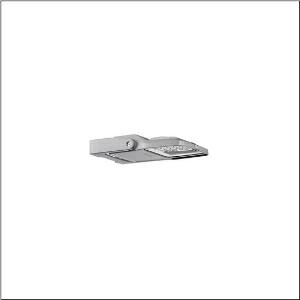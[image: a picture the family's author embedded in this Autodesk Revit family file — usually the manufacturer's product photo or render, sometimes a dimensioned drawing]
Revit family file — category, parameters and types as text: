
# Revit family: floodlight_fl_21_iq_micro___pl64_5xa7761a4e2a_05f9
name_source: partatom
category: Lighting Fixtures
units: mm (PartAtom-declared; Revit-internal decimal feet)

## family parameters
Cut with Voids When Loaded = No
Host = Face
Light Source = No
Part Type = Normal
Room Calculation Point = No
Round Connector Dimension = Use Diameter
Shared = No

## types (1)
- --- (1 x LED, 2980 lm, 23.1 W, 4000K)
    Apparent Load = 23 VA
    CIE Flux Codes = 28 80 98 100 100
    Color Rendering = 70
    Color Temperature = 4000K
    Default Elevation = 1800 mm
    Description = Floodlight FL 21 iQ micro, floodlight, primary light control with lens, of PMMA, primary optical cover: protective disc, of toughened safety glass, transparent, light distribution: PL64, light emission: direct distribution, installation type: surface-mounted, LED, High Power LED, rated luminous flux: 2.980lm, luminous efficacy: 129lm/W, light colour: 740, colour temperature: 4000K, control: optimised constant luminous flux control (CLO 2.0), Desk-Remote (wireless, voltage-free reading and setting of iQ features in the workshop via application-optimized NFC function/RFID function), Light-Fading, Smart-Wire, Night-Set, Lumen-Switch, Temp-Guard, Auto-Match, with terminal, 6-pole, mains connection: 220..240V, AC, 50/60Hz, start of lifetime: 23W, end of service life: 24W, reduction: 11W, luminaire housing, of diecast aluminium, powder-coated, Siteco® metallic grey (DB 702S), corrosivity category C5 mid according to DIN EN ISO 12944, sealing non-destructively replaceable, design bracket, of diecast aluminium, powder-coated, Siteco® metallic grey (DB 702S), protection rating (complete): IP66, insulation class (complete): insulation class II (safety insulation), certification: CE, ENEC, VDE, protection symbol: D, impact resistance: IK07, permissible operating ambient temperature: -40..+40°C, permissible operating ambient temperature for outdoor applications: -40..+50°C, standard: DIN EN 12944, LABS conformity tested according to VDMA 24364:2018-05, packaging unit: 1 piece

Light Distribution: PL64
    Height = 65 mm
    Lamp = 1 x LED
    Lamp Light Flux = 2980 lm
    Lamp Power = 23.1 W
    Lamp count = 1
    Length = 312 mm
    Luminous efficacy = 129 lm/W
    Manufacturer = Siteco
    ModVariant = No
    Model = 5XA7761A4E2A
    Mounting Place = Wall
    Mounting Type = Surface mounted
    Number of Poles = 1
    OnlyDefault = Yes
    Power Factor = 1
    Product Name = Floodlight FL 21 iQ micro | PL64
    Product group = floodlight | wall mounted
    ProductGroupID = 2001
    Protection Class = Protection class II
    Protection Degree = IP 66
    RLX_Detail_Level = 1
    RLX_Emergency_Light_Flux = 0 lm
    RLX_Emergency_Type = 0
    RLX_Emergency_Type_DB = No
    RlxData = <blob elided: 97301 chars, md5=d0be6991>
    Socket = socket
    Standby Power = 0 W
    System Light Flux = 2980 lm
    System Power = 23 W
    Type Comments = factory setting: luminous flux: 100 % | dim-lin: 254 | 455 mA
    Type Image = l_1006878.jpg
    URL = http://relux.com
    VarID = @adj_132195
    Voltage = 0 V
    Weight = 0.00 kg
    Width = 230 mm

## geometry (parser evidence)
native form markers: Blend x4, Sweep x13
no freeform markers — native parametric forms only
